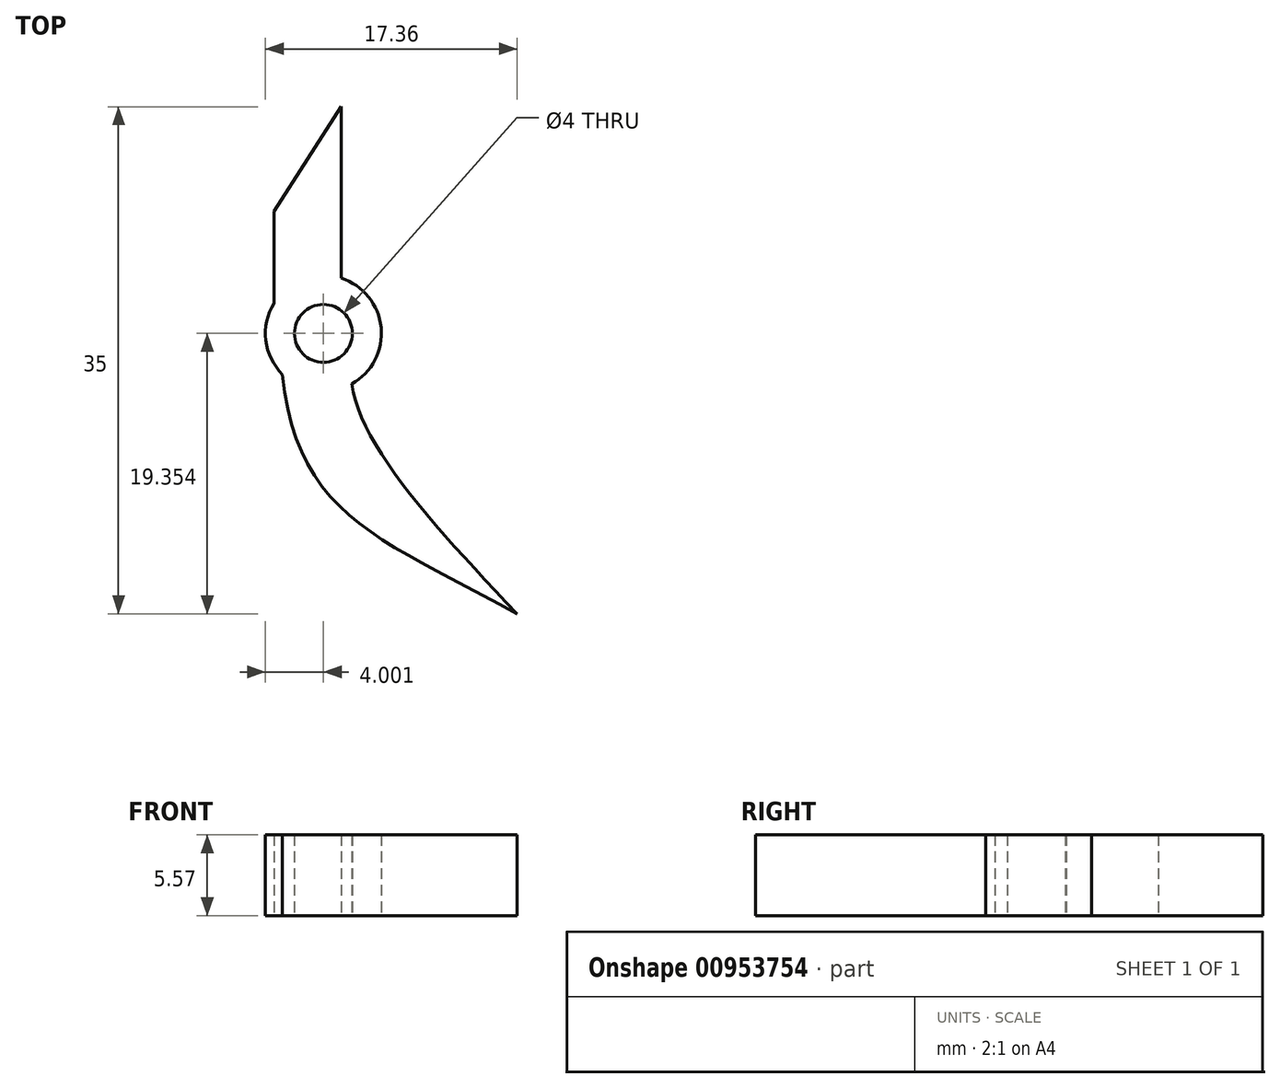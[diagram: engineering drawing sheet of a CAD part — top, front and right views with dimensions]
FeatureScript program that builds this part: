
annotation { "Feature Type Name" : "Feature", "Feature Type Description" : "" }
export const myFeature = defineFeature(function(context is Context, id is Id, definition is map)
    precondition{}
    {
        {
            var Q0;
            Q0=qCreatedBy(makeId("Top.planeOp"),FACE);
            var sketch = newSketch(context, id + "F0", { "sketchPlane" : qUnion([Q0])});
            skCircle(sketch, "E0", {"center": v(-13.36, 22.21) * mm, "radius": 4 * mm});
            skFitSpline(sketch, "E1", {"points": [v(-16.18, 19.37) * mm, v(0, 2.86) * mm], "startDerivative": vector(2.87, -29.23) * mm, "endDerivative": vector(28.09, -15.43) * mm});
            skLineSegment(sketch, "E2", {"start": v(-16.77, 24.3) * mm, "end": v(-16.77, 30.64) * mm});
            skLineSegment(sketch, "E3", {"start": v(-16.77, 30.64) * mm, "end": v(-12.14, 37.86) * mm});
            skLineSegment(sketch, "E4", {"start": v(-12.14, 37.86) * mm, "end": v(-12.14, 26.02) * mm});
            skFitSpline(sketch, "E5", {"points": [v(-11.4, 18.73) * mm, v(0, 2.86) * mm], "startDerivative": vector(1.68, -12.59) * mm, "endDerivative": vector(17.37, -18.25) * mm});
            skCircle(sketch, "E6", {"center": v(-13.36, 22.21) * mm, "radius": 2 * mm});
            skSolve(sketch);
        }
        {
            var Q0;
            {var subQ0=sQuery(id+"F0.wireOp",EDGE,"E0");var subQ1=makeQuery(id+"F0.imprint","INTERSECT",VERTEX,{"derivedFrom":[subQ0,sQuery(id+"F0.wireOp",EDGE,"E2")]});Q0=makeQuery(id+"F0.imprint","IMPRINT",FACE,{"disambiguationData":[TD([[makeQuery(id+"F0.imprint","IMPRINT",EDGE,{"disambiguationData":[TD([[subQ1,1.0]])],"derivedFrom":subQ0}),1.0]])]});}
            var Q1;
            {var subQ0=sQuery(id+"F0.wireOp",EDGE,"E2");Q1=makeQuery(id+"F0.imprint","IMPRINT",FACE,{"disambiguationData":[TD([[makeQuery(id+"F0.imprint","IMPRINT",EDGE,{"derivedFrom":subQ0}),-1.0]])]});}
            var Q2;
            {var subQ0=sQuery(id+"F0.wireOp",EDGE,"E0");var subQ1=makeQuery(id+"F0.imprint","INTERSECT",VERTEX,{"derivedFrom":[subQ0,sQuery(id+"F0.wireOp",EDGE,"E2")]});Q2=makeQuery(id+"F0.imprint","IMPRINT",FACE,{"disambiguationData":[TD([[makeQuery(id+"F0.imprint","IMPRINT",EDGE,{"disambiguationData":[TD([[subQ1,1.0]])],"derivedFrom":subQ0}),1.0]])]});}
            var Q3;
            {var subQ0=sQuery(id+"F0.wireOp",EDGE,"E1");Q3=makeQuery(id+"F0.imprint","IMPRINT",FACE,{"disambiguationData":[TD([[makeQuery(id+"F0.imprint","IMPRINT",EDGE,{"derivedFrom":subQ0}),1.0]])]});}
            extrude(context, id + "F1", {"entities" : qUnion([Q0, Q1, Q2, Q3]), "depth" : 5.57 * mm, "offsetDistance" : 25 * mm});
        }
    });
